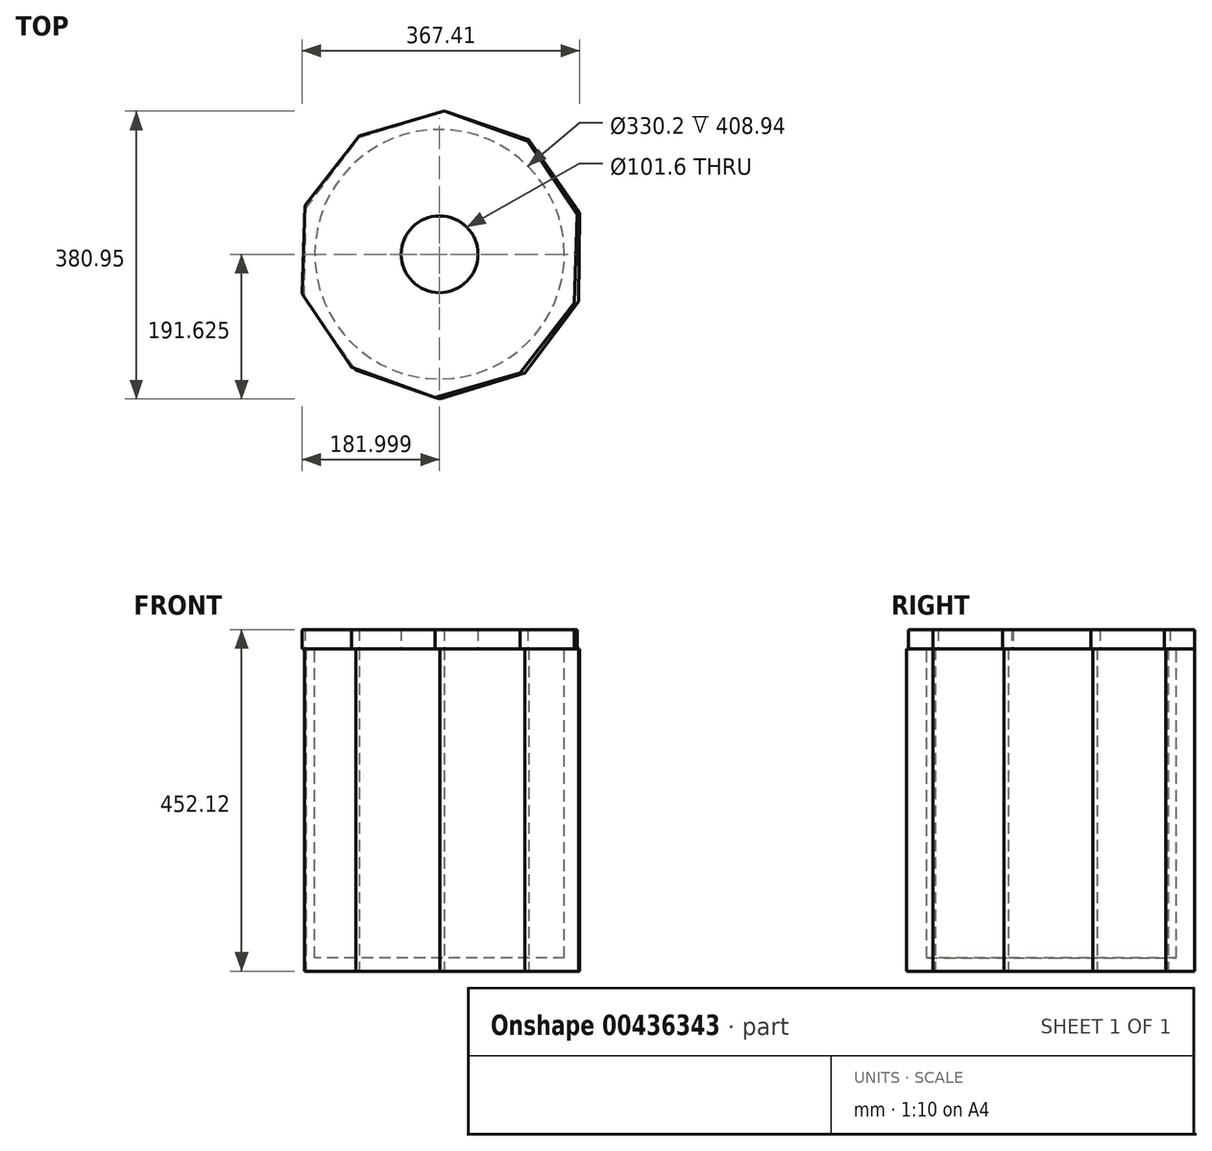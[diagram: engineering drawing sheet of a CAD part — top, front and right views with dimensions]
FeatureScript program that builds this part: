
annotation { "Feature Type Name" : "Feature", "Feature Type Description" : "" }
export const myFeature = defineFeature(function(context is Context, id is Id, definition is map)
    precondition{}
    {
        {
            var Q0;
            Q0=qCreatedBy(makeId("Top.planeOp"),FACE);
            var sketch = newSketch(context, id + "F0", { "sketchPlane" : qUnion([Q0])});
            skCircle(sketch, "E0.cCircle", {"center": v(-119.76, 19.69) * mm, "radius": 181.18 * mm, "construction": true});
            skLineSegment(sketch, "E0.0", {"start": v(60.5, -41.92) * mm, "end": v(-10.14, -136.11) * mm});
            skLineSegment(sketch, "E0.1", {"start": v(-10.14, -136.11) * mm, "end": v(-122.65, -170.8) * mm});
            skLineSegment(sketch, "E0.2", {"start": v(-122.65, -170.8) * mm, "end": v(-234.06, -132.71) * mm});
            skLineSegment(sketch, "E0.3", {"start": v(-234.06, -132.71) * mm, "end": v(-301.81, -36.42) * mm});
            skLineSegment(sketch, "E0.4", {"start": v(-301.81, -36.42) * mm, "end": v(-300.02, 81.3) * mm});
            skLineSegment(sketch, "E0.5", {"start": v(-300.02, 81.3) * mm, "end": v(-229.38, 175.49) * mm});
            skLineSegment(sketch, "E0.6", {"start": v(-229.38, 175.49) * mm, "end": v(-116.87, 210.16) * mm});
            skLineSegment(sketch, "E0.7", {"start": v(-116.87, 210.16) * mm, "end": v(-5.46, 172.09) * mm});
            skLineSegment(sketch, "E0.8", {"start": v(-5.46, 172.09) * mm, "end": v(62.29, 75.8) * mm});
            skLineSegment(sketch, "E0.9", {"start": v(62.29, 75.8) * mm, "end": v(60.5, -41.92) * mm});
            skPoint(sketch, "E0.0.midPoint", {"position": v(25.18, -89.02) * mm});
            skSolve(sketch);
        }
        {
            var Q0;
            Q0=makeQuery(id+"F0.imprint","IMPRINT",FACE,{"disambiguationData":[TD([[makeQuery(id+"F0.imprint","IMPRINT",EDGE,{"derivedFrom":sQuery(id+"F0.wireOp",EDGE,"E0.0")}),-1.0]])]});
            extrude(context, id + "F1", {"entities" : qUnion([Q0]), "depth" : 426.72 * mm});
        }
        {
            var Q0;
            Q0=makeQuery(id+"F1.opExtrude","CAP_FACE",FACE,{"disambiguationData":[OSD([sQuery(id+"F0.wireOp",EDGE,"E0.0"),sQuery(id+"F0.wireOp",EDGE,"E0.1"),sQuery(id+"F0.wireOp",EDGE,"E0.2"),sQuery(id+"F0.wireOp",EDGE,"E0.3"),sQuery(id+"F0.wireOp",EDGE,"E0.4"),sQuery(id+"F0.wireOp",EDGE,"E0.5"),sQuery(id+"F0.wireOp",EDGE,"E0.6"),sQuery(id+"F0.wireOp",EDGE,"E0.7"),sQuery(id+"F0.wireOp",EDGE,"E0.8"),sQuery(id+"F0.wireOp",EDGE,"E0.9")])],"isStart":false});
            var sketch = newSketch(context, id + "F2", { "sketchPlane" : qUnion([Q0])});
            skCircle(sketch, "E1", {"center": v(-123.12, 20.83) * mm, "radius": 165.1 * mm});
            skSolve(sketch);
        }
        {
            var Q0;
            Q0=makeQuery(id+"F2.imprint","IMPRINT",FACE,{"disambiguationData":[TD([[makeQuery(id+"F2.imprint","IMPRINT",EDGE,{"derivedFrom":sQuery(id+"F2.wireOp",EDGE,"E1")}),1.0]])]});
            extrude(context, id + "F3", {"entities" : qUnion([Q0]), "operationType" : NewBodyOperationType.REMOVE, "oppositeDirection" : true, "depth" : 408.94 * mm});
        }
        {
            var Q0;
            Q0=makeQuery(id+"F2.imprint","IMPRINT",FACE,{"disambiguationData":[TD([[makeQuery(id+"F2.imprint","IMPRINT",EDGE,{"derivedFrom":sQuery(id+"F2.wireOp",EDGE,"E1")}),-1.0]])]});
            var sketch = newSketch(context, id + "F4", { "sketchPlane" : qUnion([Q0])});
            skCircle(sketch, "E2.cCircle", {"center": v(-123.12, 20.83) * mm, "radius": 180.16 * mm, "construction": true});
            skLineSegment(sketch, "E2.0", {"start": v(-116.87, 210.16) * mm, "end": v(-6.78, 170.33) * mm});
            skLineSegment(sketch, "E2.1", {"start": v(-6.78, 170.33) * mm, "end": v(58.87, 73.4) * mm});
            skLineSegment(sketch, "E2.2", {"start": v(58.87, 73.4) * mm, "end": v(55.01, -43.62) * mm});
            skLineSegment(sketch, "E2.3", {"start": v(55.01, -43.62) * mm, "end": v(-16.9, -136.01) * mm});
            skLineSegment(sketch, "E2.4", {"start": v(-16.9, -136.01) * mm, "end": v(-129.37, -168.5) * mm});
            skLineSegment(sketch, "E2.5", {"start": v(-129.37, -168.5) * mm, "end": v(-239.46, -128.66) * mm});
            skLineSegment(sketch, "E2.6", {"start": v(-239.46, -128.66) * mm, "end": v(-305.12, -31.73) * mm});
            skLineSegment(sketch, "E2.7", {"start": v(-305.12, -31.73) * mm, "end": v(-301.25, 85.29) * mm});
            skLineSegment(sketch, "E2.8", {"start": v(-301.25, 85.29) * mm, "end": v(-229.35, 177.68) * mm});
            skLineSegment(sketch, "E2.9", {"start": v(-229.35, 177.68) * mm, "end": v(-116.87, 210.16) * mm});
            skPoint(sketch, "E2.0.midPoint", {"position": v(-61.82, 190.25) * mm});
            skCircle(sketch, "E3", {"center": v(-123.12, 20.83) * mm, "radius": 50.8 * mm});
            skSolve(sketch);
        }
        {
            var Q0;
            Q0 = qSketchRegion(id + "F4", true);
            extrude(context, id + "F5", {"entities" : qUnion([Q0]), "operationType" : NewBodyOperationType.ADD, "depth" : 25.4 * mm});
        }
        {
            var Q0;
            Q0=makeQuery(id+"F5.opExtrude","CAP_FACE",FACE,{"disambiguationData":[OSD([sQuery(id+"F4.wireOp",EDGE,"E2.0"),sQuery(id+"F4.wireOp",EDGE,"E2.1"),sQuery(id+"F4.wireOp",EDGE,"E2.2"),sQuery(id+"F4.wireOp",EDGE,"E2.3"),sQuery(id+"F4.wireOp",EDGE,"E2.4"),sQuery(id+"F4.wireOp",EDGE,"E2.5"),sQuery(id+"F4.wireOp",EDGE,"E2.6"),sQuery(id+"F4.wireOp",EDGE,"E2.7"),sQuery(id+"F4.wireOp",EDGE,"E2.8"),sQuery(id+"F4.wireOp",EDGE,"E2.9"),sQuery(id+"F4.wireOp",EDGE,"E3")])],"isStart":false});
            extrude(context, id + "F6", {"entities" : qUnion([Q0]), "operationType" : NewBodyOperationType.ADD, "oppositeDirection" : true, "depth" : 23.62 * mm});
        }
    });
